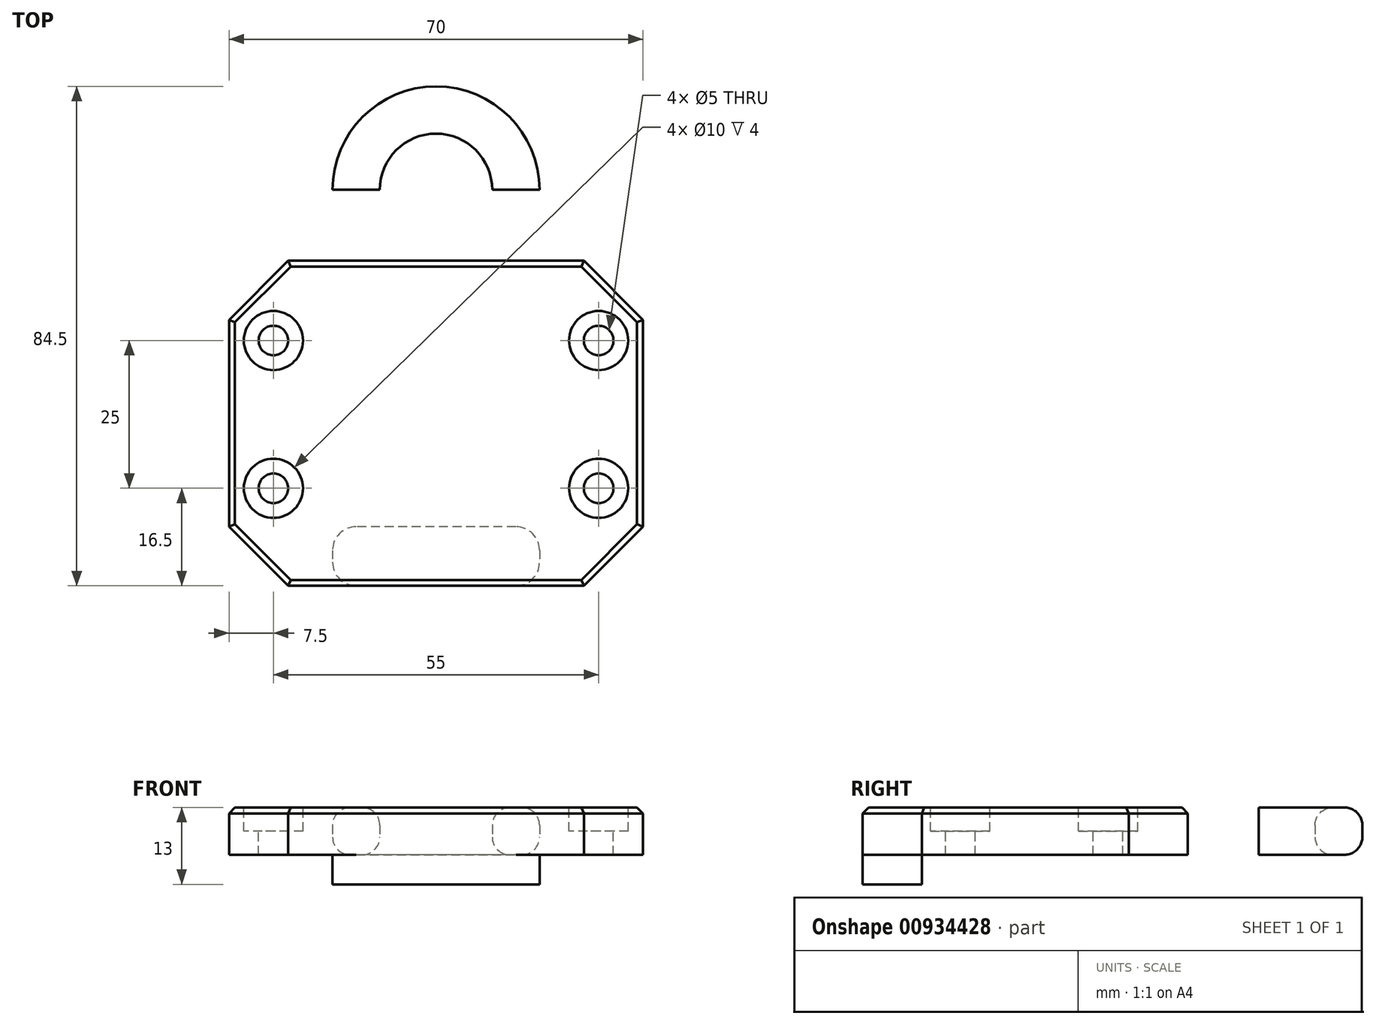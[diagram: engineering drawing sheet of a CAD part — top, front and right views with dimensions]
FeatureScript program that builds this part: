
annotation { "Feature Type Name" : "Feature", "Feature Type Description" : "" }
export const myFeature = defineFeature(function(context is Context, id is Id, definition is map)
    precondition{}
    {
        {
            var Q0;
            Q0=qCreatedBy(makeId("Top.planeOp"),FACE);
            var sketch = newSketch(context, id + "F0", { "sketchPlane" : qUnion([Q0])});
            skLineSegment(sketch, "E0.bottom", {"start": v(17.5, 28.5) * mm, "end": v(-17.5, 28.5) * mm});
            skLineSegment(sketch, "E0.top", {"start": v(17.5, -28.5) * mm, "end": v(-17.5, -28.5) * mm});
            skLineSegment(sketch, "E0.left", {"start": v(17.5, 28.5) * mm, "end": v(17.5, -28.5) * mm});
            skLineSegment(sketch, "E0.right", {"start": v(-17.5, 28.5) * mm, "end": v(-17.5, -28.5) * mm});
            skPoint(sketch, "E0.middle", {"position": v(0, 0) * mm});
            skLineSegment(sketch, "E1.bottom", {"start": v(-17.5, -28.5) * mm, "end": v(17.5, -28.5) * mm});
            skLineSegment(sketch, "E1.top", {"start": v(-17.5, -38.5) * mm, "end": v(17.5, -38.5) * mm});
            skLineSegment(sketch, "E1.left", {"start": v(-17.5, -28.5) * mm, "end": v(-17.5, -38.5) * mm});
            skLineSegment(sketch, "E1.right", {"start": v(17.5, -28.5) * mm, "end": v(17.5, -38.5) * mm});
            skArc(sketch, "E2", {"start": v(17.5, 28.5) * mm, "mid": v(0, 46) * mm, "end": v(-17.5, 28.5) * mm});
            skCircle(sketch, "E3", {"center": v(0, 28.5) * mm, "radius": 9.5 * mm});
            skLineSegment(sketch, "E4.bottom", {"start": v(-35, -38.5) * mm, "end": v(35, -38.5) * mm});
            skLineSegment(sketch, "E4.top", {"start": v(-35, 16.5) * mm, "end": v(35, 16.5) * mm});
            skLineSegment(sketch, "E4.left", {"start": v(-35, -38.5) * mm, "end": v(-35, 16.5) * mm});
            skLineSegment(sketch, "E4.right", {"start": v(35, -38.5) * mm, "end": v(35, 16.5) * mm});
            skSolve(sketch);
        }
        {
            var Q0;
            {var subQ4=sQuery(id+"F0.wireOp",EDGE,"E1.left");Q0=makeQuery(id+"F0.imprint","IMPRINT",FACE,{"disambiguationData":[TD([[makeQuery(id+"F0.imprint","IMPRINT",EDGE,{"derivedFrom":subQ4}),-1.0]])]});}
            var Q1;
            {var subQ0=sQuery(id+"F0.wireOp",EDGE,"E0.top");Q1=makeQuery(id+"F0.imprint","IMPRINT",FACE,{"disambiguationData":[TD([[makeQuery(id+"F0.imprint","IMPRINT",EDGE,{"derivedFrom":subQ0}),-1.0]])]});}
            var Q2;
            {var subQ5=sQuery(id+"F0.wireOp",EDGE,"E1.right");Q2=makeQuery(id+"F0.imprint","IMPRINT",FACE,{"disambiguationData":[TD([[makeQuery(id+"F0.imprint","IMPRINT",EDGE,{"derivedFrom":subQ5}),1.0]])]});}
            var Q3;
            Q3=makeQuery(id+"F0.imprint","IMPRINT",FACE,{"disambiguationData":[TD([[makeQuery(id+"F0.imprint","IMPRINT",EDGE,{"derivedFrom":sQuery(id+"F0.wireOp",EDGE,"E0.top")}),1.0]])]});
            var Q4;
            {var subQ3=sQuery(id+"F0.wireOp",EDGE,"E2");Q4=makeQuery(id+"F0.imprint","IMPRINT",FACE,{"disambiguationData":[TD([[makeQuery(id+"F0.imprint","IMPRINT",EDGE,{"derivedFrom":subQ3}),1.0]])]});}
            var Q5;
            {var subQ4=sQuery(id+"F0.wireOp",EDGE,"E0.bottom");var subQ9=sQuery(id+"F0.wireOp",EDGE,"E3");var subQ11=makeQuery(id+"F0.imprint","INTERSECT",VERTEX,{"disambiguationData":[OD(0.0)],"derivedFrom":[subQ4,subQ9]});Q5=makeQuery(id+"F0.imprint","IMPRINT",FACE,{"disambiguationData":[TD([[makeQuery(id+"F0.imprint","IMPRINT",EDGE,{"disambiguationData":[TD([[subQ11,1.0]])],"derivedFrom":subQ9}),-1.0]])]});}
            var Q6;
            {var subQ4=sQuery(id+"F0.wireOp",EDGE,"E0.bottom");var subQ9=sQuery(id+"F0.wireOp",EDGE,"E3");var subQ11=makeQuery(id+"F0.imprint","INTERSECT",VERTEX,{"disambiguationData":[OD(0.0)],"derivedFrom":[subQ4,subQ9]});Q6=makeQuery(id+"F0.imprint","IMPRINT",FACE,{"disambiguationData":[TD([[makeQuery(id+"F0.imprint","IMPRINT",EDGE,{"disambiguationData":[TD([[subQ11,1.0]])],"derivedFrom":subQ9}),-1.0]])]});}
            extrude(context, id + "F1", {"entities" : qUnion([Q0, Q1, Q2, Q3, Q4, Q5, Q6]), "depth" : 8 * mm, "offsetDistance" : 25 * mm});
        }
        {
            var Q0;
            Q0=makeQuery(id+"F0.imprint","IMPRINT",FACE,{"disambiguationData":[TD([[makeQuery(id+"F0.imprint","IMPRINT",EDGE,{"derivedFrom":sQuery(id+"F0.wireOp",EDGE,"E0.top")}),1.0]])]});
            extrude(context, id + "F2", {"entities" : qUnion([Q0]), "operationType" : NewBodyOperationType.ADD, "oppositeDirection" : true, "depth" : 5 * mm, "offsetDistance" : 25 * mm});
        }
        {
            var Q0;
            Q0=makeQuery(id+"F2.opExtrude","SWEPT_EDGE",EDGE,{"disambiguationData":[OSD([sQuery(id+"F0.wireOp",EDGE,"E0.top"),sQuery(id+"F0.wireOp",EDGE,"E0.left"),sQuery(id+"F0.wireOp",EDGE,"E1.right")])]});
            var Q1;
            Q1=makeQuery(id+"F2.opExtrude","SWEPT_EDGE",EDGE,{"disambiguationData":[OSD([sQuery(id+"F0.wireOp",EDGE,"E1.top"),sQuery(id+"F0.wireOp",EDGE,"E1.right"),sQuery(id+"F0.wireOp",EDGE,"E4.bottom")])]});
            var Q2;
            Q2=makeQuery(id+"F2.opExtrude","SWEPT_EDGE",EDGE,{"disambiguationData":[OSD([sQuery(id+"F0.wireOp",EDGE,"E0.top"),sQuery(id+"F0.wireOp",EDGE,"E0.right"),sQuery(id+"F0.wireOp",EDGE,"E1.left")])]});
            var Q3;
            Q3=makeQuery(id+"F2.opExtrude","SWEPT_EDGE",EDGE,{"disambiguationData":[OSD([sQuery(id+"F0.wireOp",EDGE,"E1.top"),sQuery(id+"F0.wireOp",EDGE,"E1.left"),sQuery(id+"F0.wireOp",EDGE,"E4.bottom")])]});
            fillet(context, id + "F3", {"entities" : qUnion([Q0, Q1, Q2, Q3]), "radius" : 4 * mm, "tangentPropagation" : true, "allowEdgeOverflow" : false});
        }
        {
            var Q0;
            Q0=makeQuery(id+"F1.opExtrude","CAP_EDGE",EDGE,{"disambiguationData":[OSD([sQuery(id+"F0.wireOp",EDGE,"E2")])],"isStart":false});
            var Q1;
            Q1=makeQuery(id+"F1.opExtrude","CAP_EDGE",EDGE,{"disambiguationData":[OSD([sQuery(id+"F0.wireOp",EDGE,"E2")])],"isStart":true});
            var Q2;
            Q2=makeQuery(id+"F1.opExtrude","CAP_EDGE",EDGE,{"disambiguationData":[OSD([sQuery(id+"F0.wireOp",EDGE,"E3")])],"isStart":true});
            var Q3;
            Q3=makeQuery(id+"F1.opExtrude","CAP_EDGE",EDGE,{"disambiguationData":[OSD([sQuery(id+"F0.wireOp",EDGE,"E3")])],"isStart":false});
            fillet(context, id + "F4", {"entities" : qUnion([Q0, Q1, Q2, Q3]), "radius" : 3 * mm, "tangentPropagation" : true, "allowEdgeOverflow" : false});
        }
        {
            var Q0;
            Q0=makeQuery(id+"F1.opExtrude","SWEPT_EDGE",EDGE,{"disambiguationData":[OSD([sQuery(id+"F0.wireOp",EDGE,"E4.top"),sQuery(id+"F0.wireOp",EDGE,"E4.left")])]});
            var Q1;
            Q1=makeQuery(id+"F1.opExtrude","SWEPT_EDGE",EDGE,{"disambiguationData":[OSD([sQuery(id+"F0.wireOp",EDGE,"E4.top"),sQuery(id+"F0.wireOp",EDGE,"E4.right")])]});
            var Q2;
            Q2=makeQuery(id+"F1.opExtrude","SWEPT_EDGE",EDGE,{"disambiguationData":[OSD([sQuery(id+"F0.wireOp",EDGE,"E4.bottom"),sQuery(id+"F0.wireOp",EDGE,"E4.right")])]});
            var Q3;
            Q3=makeQuery(id+"F1.opExtrude","SWEPT_EDGE",EDGE,{"disambiguationData":[OSD([sQuery(id+"F0.wireOp",EDGE,"E4.bottom"),sQuery(id+"F0.wireOp",EDGE,"E4.left")])]});
            chamfer(context, id + "F5", {"entities" : qUnion([Q0, Q1, Q2, Q3]), "width" : 10 * mm, "tangentPropagation" : true});
        }
        {
            var Q0;
            Q0=makeQuery(id+"F1.opExtrude","CAP_FACE",FACE,{"disambiguationData":[OSD([sQuery(id+"F0.wireOp",EDGE,"E0.left"),sQuery(id+"F0.wireOp",EDGE,"E0.right"),sQuery(id+"F0.wireOp",EDGE,"E1.top"),sQuery(id+"F0.wireOp",EDGE,"E2"),sQuery(id+"F0.wireOp",EDGE,"E3"),sQuery(id+"F0.wireOp",EDGE,"E4.bottom"),sQuery(id+"F0.wireOp",EDGE,"E4.top"),sQuery(id+"F0.wireOp",EDGE,"E4.left"),sQuery(id+"F0.wireOp",EDGE,"E4.right")])],"isStart":false});
            var sketch = newSketch(context, id + "F6", { "sketchPlane" : qUnion([Q0])});
            skPoint(sketch, "E5", {"position": v(-27.5, -22) * mm});
            skPoint(sketch, "E6", {"position": v(-27.5, 3) * mm});
            skPoint(sketch, "E7", {"position": v(27.5, -22) * mm});
            skPoint(sketch, "E8", {"position": v(27.5, 3) * mm});
            skSolve(sketch);
        }
        {
            var Q0;
            Q0=sQuery(id+"F6.wireOp",VERTEX,"E6");
            var Q1;
            Q1=sQuery(id+"F6.wireOp",VERTEX,"E8");
            var Q2;
            Q2=sQuery(id+"F6.wireOp",VERTEX,"E7");
            var Q3;
            Q3=sQuery(id+"F6.wireOp",VERTEX,"E5");
            var Q4;
            Q4=makeQuery(id+"F1.opExtrude","SWEPT_BODY",BODY,{"disambiguationData":[OSD([sQuery(id+"F0.wireOp",EDGE,"E0.left"),sQuery(id+"F0.wireOp",EDGE,"E0.right"),sQuery(id+"F0.wireOp",EDGE,"E1.top"),sQuery(id+"F0.wireOp",EDGE,"E2"),sQuery(id+"F0.wireOp",EDGE,"E3"),sQuery(id+"F0.wireOp",EDGE,"E4.bottom"),sQuery(id+"F0.wireOp",EDGE,"E4.top"),sQuery(id+"F0.wireOp",EDGE,"E4.left"),sQuery(id+"F0.wireOp",EDGE,"E4.right")])]});
            hole(context, id + "F7", {"style" : HoleStyle.C_BORE, "endStyle" : HoleEndStyle.BLIND, "holeDiameter" : 5 * mm, "cBoreDiameter" : 10 * mm, "cBoreDepth" : 4 * mm, "majorDiameter" : 5 * mm, "holeDepth" : 18 * mm, "isTappedThrough" : true, "tappedDepth" : 12 * mm, "tapClearance" : 3, "locations" : qUnion([Q0, Q1, Q2, Q3]), "scope" : qUnion([Q4])});
        }
        {
            var Q0;
            Q0=makeQuery(id+"F1.opExtrude","CAP_EDGE",EDGE,{"disambiguationData":[OSD([sQuery(id+"F0.wireOp",EDGE,"E4.left")])],"isStart":false});
            var Q1;
            {var subQ0=sQuery(id+"F0.wireOp",EDGE,"E4.left");var subQ1=sQuery(id+"F0.wireOp",EDGE,"E4.top");Q1=makeQuery(id+"F5.opChamfer","BLEND_EDGE",EDGE,{"blendedFrom":[makeQuery(id+"F1.opExtrude","SWEPT_EDGE",EDGE,{"disambiguationData":[OSD([subQ1,subQ0])]}),makeQuery(id+"F1.opExtrude","CAP_FACE",FACE,{"disambiguationData":[OSD([sQuery(id+"F0.wireOp",EDGE,"E0.left"),sQuery(id+"F0.wireOp",EDGE,"E0.right"),sQuery(id+"F0.wireOp",EDGE,"E1.top"),sQuery(id+"F0.wireOp",EDGE,"E2"),sQuery(id+"F0.wireOp",EDGE,"E3"),sQuery(id+"F0.wireOp",EDGE,"E4.bottom"),subQ1,subQ0,sQuery(id+"F0.wireOp",EDGE,"E4.right")])],"isStart":false})],"blendedInto":[makeQuery(id+"F1.opExtrude","CAP_FACE",FACE,{"disambiguationData":[OSD([sQuery(id+"F0.wireOp",EDGE,"E0.left"),sQuery(id+"F0.wireOp",EDGE,"E0.right"),sQuery(id+"F0.wireOp",EDGE,"E1.top"),sQuery(id+"F0.wireOp",EDGE,"E2"),sQuery(id+"F0.wireOp",EDGE,"E3"),sQuery(id+"F0.wireOp",EDGE,"E4.bottom"),subQ1,subQ0,sQuery(id+"F0.wireOp",EDGE,"E4.right")])],"isStart":false})]});}
            var Q2;
            {var subQ0=sQuery(id+"F0.wireOp",EDGE,"E4.left");var subQ1=sQuery(id+"F0.wireOp",EDGE,"E4.bottom");Q2=makeQuery(id+"F5.opChamfer","BLEND_EDGE",EDGE,{"blendedFrom":[makeQuery(id+"F1.opExtrude","SWEPT_EDGE",EDGE,{"disambiguationData":[OSD([subQ1,subQ0])]}),makeQuery(id+"F1.opExtrude","CAP_FACE",FACE,{"disambiguationData":[OSD([sQuery(id+"F0.wireOp",EDGE,"E0.left"),sQuery(id+"F0.wireOp",EDGE,"E0.right"),sQuery(id+"F0.wireOp",EDGE,"E1.top"),sQuery(id+"F0.wireOp",EDGE,"E2"),sQuery(id+"F0.wireOp",EDGE,"E3"),subQ1,sQuery(id+"F0.wireOp",EDGE,"E4.top"),subQ0,sQuery(id+"F0.wireOp",EDGE,"E4.right")])],"isStart":false})],"blendedInto":[makeQuery(id+"F1.opExtrude","CAP_FACE",FACE,{"disambiguationData":[OSD([sQuery(id+"F0.wireOp",EDGE,"E0.left"),sQuery(id+"F0.wireOp",EDGE,"E0.right"),sQuery(id+"F0.wireOp",EDGE,"E1.top"),sQuery(id+"F0.wireOp",EDGE,"E2"),sQuery(id+"F0.wireOp",EDGE,"E3"),subQ1,sQuery(id+"F0.wireOp",EDGE,"E4.top"),subQ0,sQuery(id+"F0.wireOp",EDGE,"E4.right")])],"isStart":false})]});}
            var Q3;
            Q3=makeQuery(id+"F1.opExtrude","CAP_EDGE",EDGE,{"disambiguationData":[OSD([sQuery(id+"F0.wireOp",EDGE,"E1.top"),sQuery(id+"F0.wireOp",EDGE,"E4.bottom")])],"isStart":false});
            var Q4;
            {var subQ0=sQuery(id+"F0.wireOp",EDGE,"E4.right");var subQ1=sQuery(id+"F0.wireOp",EDGE,"E4.bottom");Q4=makeQuery(id+"F5.opChamfer","BLEND_EDGE",EDGE,{"blendedFrom":[makeQuery(id+"F1.opExtrude","SWEPT_EDGE",EDGE,{"disambiguationData":[OSD([subQ1,subQ0])]}),makeQuery(id+"F1.opExtrude","CAP_FACE",FACE,{"disambiguationData":[OSD([sQuery(id+"F0.wireOp",EDGE,"E0.left"),sQuery(id+"F0.wireOp",EDGE,"E0.right"),sQuery(id+"F0.wireOp",EDGE,"E1.top"),sQuery(id+"F0.wireOp",EDGE,"E2"),sQuery(id+"F0.wireOp",EDGE,"E3"),subQ1,sQuery(id+"F0.wireOp",EDGE,"E4.top"),sQuery(id+"F0.wireOp",EDGE,"E4.left"),subQ0])],"isStart":false})],"blendedInto":[makeQuery(id+"F1.opExtrude","CAP_FACE",FACE,{"disambiguationData":[OSD([sQuery(id+"F0.wireOp",EDGE,"E0.left"),sQuery(id+"F0.wireOp",EDGE,"E0.right"),sQuery(id+"F0.wireOp",EDGE,"E1.top"),sQuery(id+"F0.wireOp",EDGE,"E2"),sQuery(id+"F0.wireOp",EDGE,"E3"),subQ1,sQuery(id+"F0.wireOp",EDGE,"E4.top"),sQuery(id+"F0.wireOp",EDGE,"E4.left"),subQ0])],"isStart":false})]});}
            var Q5;
            Q5=makeQuery(id+"F1.opExtrude","CAP_EDGE",EDGE,{"disambiguationData":[OSD([sQuery(id+"F0.wireOp",EDGE,"E4.right")])],"isStart":false});
            var Q6;
            {var subQ0=sQuery(id+"F0.wireOp",EDGE,"E4.right");var subQ1=sQuery(id+"F0.wireOp",EDGE,"E4.top");Q6=makeQuery(id+"F5.opChamfer","BLEND_EDGE",EDGE,{"blendedFrom":[makeQuery(id+"F1.opExtrude","SWEPT_EDGE",EDGE,{"disambiguationData":[OSD([subQ1,subQ0])]}),makeQuery(id+"F1.opExtrude","CAP_FACE",FACE,{"disambiguationData":[OSD([sQuery(id+"F0.wireOp",EDGE,"E0.left"),sQuery(id+"F0.wireOp",EDGE,"E0.right"),sQuery(id+"F0.wireOp",EDGE,"E1.top"),sQuery(id+"F0.wireOp",EDGE,"E2"),sQuery(id+"F0.wireOp",EDGE,"E3"),sQuery(id+"F0.wireOp",EDGE,"E4.bottom"),subQ1,sQuery(id+"F0.wireOp",EDGE,"E4.left"),subQ0])],"isStart":false})],"blendedInto":[makeQuery(id+"F1.opExtrude","CAP_FACE",FACE,{"disambiguationData":[OSD([sQuery(id+"F0.wireOp",EDGE,"E0.left"),sQuery(id+"F0.wireOp",EDGE,"E0.right"),sQuery(id+"F0.wireOp",EDGE,"E1.top"),sQuery(id+"F0.wireOp",EDGE,"E2"),sQuery(id+"F0.wireOp",EDGE,"E3"),sQuery(id+"F0.wireOp",EDGE,"E4.bottom"),subQ1,sQuery(id+"F0.wireOp",EDGE,"E4.left"),subQ0])],"isStart":false})]});}
            var Q7;
            {var subQ0=sQuery(id+"F0.wireOp",EDGE,"E4.top");Q7=makeQuery(id+"F1.opExtrude","CAP_EDGE",EDGE,{"disambiguationData":[OSD([subQ0]),TDD([makeQuery(id+"F0.imprint","IMPRINT",EDGE,{"disambiguationData":[TD([[makeQuery(id+"F0.imprint","INTERSECT",VERTEX,{"derivedFrom":[sQuery(id+"F0.wireOp",EDGE,"E0.left"),subQ0]}),-1.0]])],"derivedFrom":subQ0})])],"isStart":false});}
            var Q8;
            {var subQ0=sQuery(id+"F0.wireOp",EDGE,"E4.top");Q8=makeQuery(id+"F1.opExtrude","CAP_EDGE",EDGE,{"disambiguationData":[OSD([subQ0]),TDD([makeQuery(id+"F0.imprint","IMPRINT",EDGE,{"disambiguationData":[TD([[makeQuery(id+"F0.imprint","INTERSECT",VERTEX,{"derivedFrom":[sQuery(id+"F0.wireOp",EDGE,"E0.right"),subQ0]}),1.0]])],"derivedFrom":subQ0})])],"isStart":false});}
            chamfer(context, id + "F8", {"entities" : qUnion([Q0, Q1, Q2, Q3, Q4, Q5, Q6, Q7, Q8]), "width" : 1 * mm, "tangentPropagation" : true});
        }
    });
